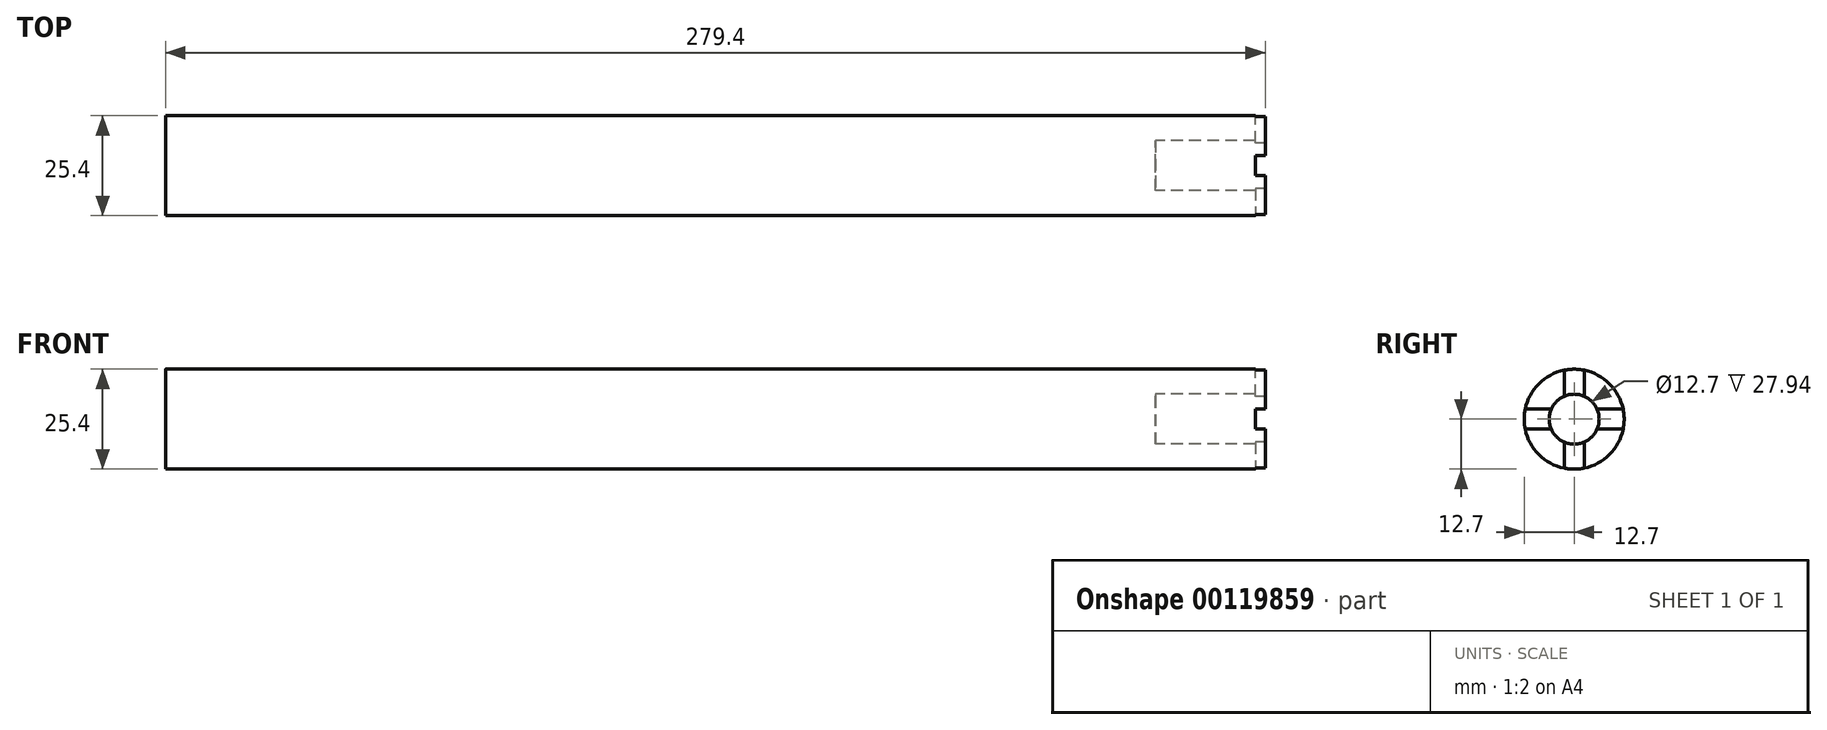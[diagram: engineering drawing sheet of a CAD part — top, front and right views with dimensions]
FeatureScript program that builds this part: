
annotation { "Feature Type Name" : "Feature", "Feature Type Description" : "" }
export const myFeature = defineFeature(function(context is Context, id is Id, definition is map)
    precondition{}
    {
        {
            var Q0;
            Q0=qCreatedBy(makeId("Right.planeOp"),FACE);
            var sketch = newSketch(context, id + "F0", { "sketchPlane" : qUnion([Q0])});
            skCircle(sketch, "E0", {"center": v(0, 0) * mm, "radius": 12.7 * mm});
            skSolve(sketch);
        }
        {
            var Q0;
            Q0 = qSketchRegion(id + "F0", true);
            var Q1;
            Q1=makeQuery(id+"F0.imprint","IMPRINT",FACE,{"disambiguationData":[TD([[makeQuery(id+"F0.imprint","IMPRINT",EDGE,{"derivedFrom":sQuery(id+"F0.wireOp",EDGE,"E0")}),1.0]])]});
            extrude(context, id + "F1", {"entities" : qUnion([Q0, Q1]), "depth" : 276.86 * mm});
        }
        {
            var Q0;
            Q0=makeQuery(id+"F1.opExtrude","CAP_FACE",FACE,{"disambiguationData":[OSD([sQuery(id+"F0.wireOp",EDGE,"E0")])],"isStart":false});
            var sketch = newSketch(context, id + "F2", { "sketchPlane" : qUnion([Q0])});
            skCircle(sketch, "E1", {"center": v(0, 0) * mm, "radius": 6.35 * mm});
            skLineSegment(sketch, "E2", {"start": v(0, 12.7) * mm, "end": v(0, 6.35) * mm, "construction": true});
            skLineSegment(sketch, "E3", {"start": v(-12.7, 0) * mm, "end": v(-6.35, 0) * mm, "construction": true});
            skLineSegment(sketch, "E4", {"start": v(-2.54, -5.82) * mm, "end": v(-2.54, -12.44) * mm});
            skLineSegment(sketch, "E5", {"start": v(2.54, -5.82) * mm, "end": v(2.54, -12.44) * mm});
            skLineSegment(sketch, "E6", {"start": v(-2.54, 5.82) * mm, "end": v(-2.54, 12.44) * mm});
            skLineSegment(sketch, "E7", {"start": v(2.54, 5.82) * mm, "end": v(2.54, 12.44) * mm});
            skLineSegment(sketch, "E8", {"start": v(5.82, 2.54) * mm, "end": v(12.44, 2.54) * mm});
            skLineSegment(sketch, "E9", {"start": v(5.82, -2.54) * mm, "end": v(12.44, -2.54) * mm});
            skLineSegment(sketch, "E10", {"start": v(-5.82, 2.54) * mm, "end": v(-12.44, 2.54) * mm});
            skLineSegment(sketch, "E11", {"start": v(-5.82, -2.54) * mm, "end": v(-12.44, -2.54) * mm});
            skLineSegment(sketch, "E12.trimOffspring", {"start": v(0, -6.35) * mm, "end": v(0, -12.7) * mm, "construction": true});
            skLineSegment(sketch, "E13.trimOffspring", {"start": v(6.35, 0) * mm, "end": v(12.7, 0) * mm, "construction": true});
            skSolve(sketch);
        }
        {
            var Q0;
            {var subQ0=sQuery(id+"F2.wireOp",EDGE,"E7");Q0=makeQuery(id+"F2.imprint","IMPRINT",FACE,{"disambiguationData":[TD([[makeQuery(id+"F2.imprint","IMPRINT",EDGE,{"derivedFrom":subQ0}),-1.0]])]});}
            var Q1;
            {var subQ0=sQuery(id+"F2.wireOp",EDGE,"E6");Q1=makeQuery(id+"F2.imprint","IMPRINT",FACE,{"disambiguationData":[TD([[makeQuery(id+"F2.imprint","IMPRINT",EDGE,{"derivedFrom":subQ0}),1.0]])]});}
            var Q2;
            {var subQ0=sQuery(id+"F2.wireOp",EDGE,"E4");Q2=makeQuery(id+"F2.imprint","IMPRINT",FACE,{"disambiguationData":[TD([[makeQuery(id+"F2.imprint","IMPRINT",EDGE,{"derivedFrom":subQ0}),-1.0]])]});}
            var Q3;
            {var subQ0=sQuery(id+"F2.wireOp",EDGE,"E5");Q3=makeQuery(id+"F2.imprint","IMPRINT",FACE,{"disambiguationData":[TD([[makeQuery(id+"F2.imprint","IMPRINT",EDGE,{"derivedFrom":subQ0}),1.0]])]});}
            extrude(context, id + "F3", {"entities" : qUnion([Q0, Q1, Q2, Q3]), "operationType" : NewBodyOperationType.ADD, "depth" : 2.54 * mm});
        }
        {
            var Q0;
            {var subQ0=sQuery(id+"F2.wireOp",EDGE,"E1");var subQ4=makeQuery(id+"F2.imprint","INTERSECT",VERTEX,{"derivedFrom":[subQ0,sQuery(id+"F2.wireOp",EDGE,"E7")]});Q0=makeQuery(id+"F2.imprint","IMPRINT",FACE,{"disambiguationData":[TD([[makeQuery(id+"F2.imprint","IMPRINT",EDGE,{"disambiguationData":[TD([[subQ4,1.0]])],"derivedFrom":subQ0}),1.0]])]});}
            extrude(context, id + "F4", {"entities" : qUnion([Q0]), "operationType" : NewBodyOperationType.REMOVE, "oppositeDirection" : true, "depth" : 25.4 * mm});
        }
    });
